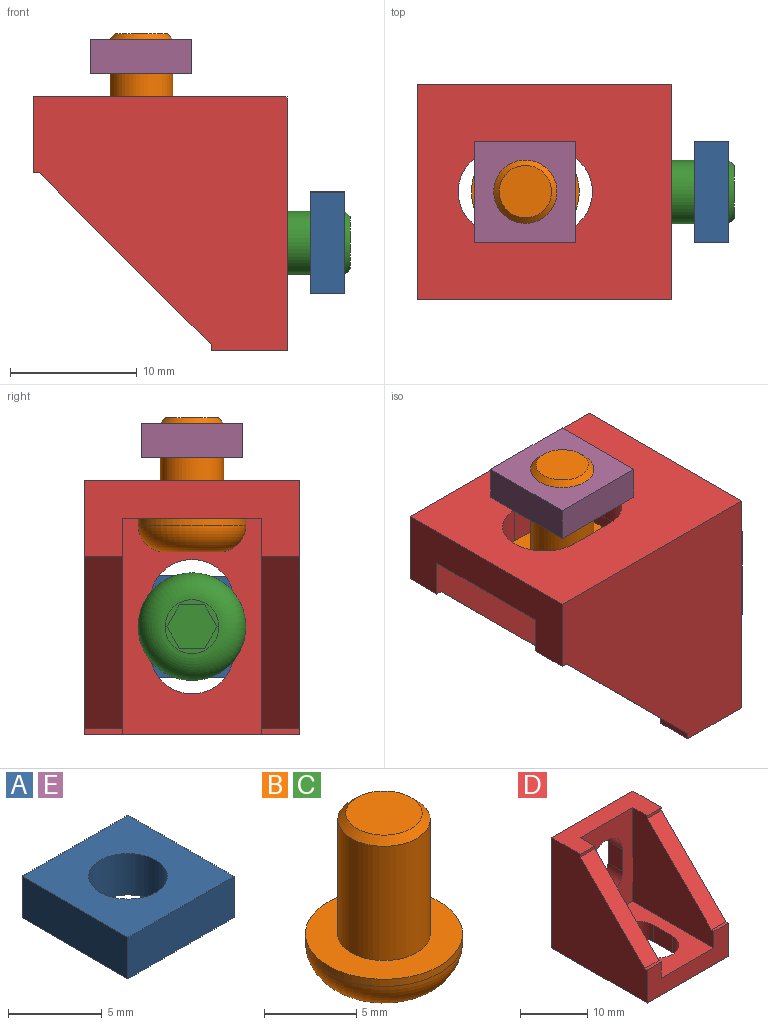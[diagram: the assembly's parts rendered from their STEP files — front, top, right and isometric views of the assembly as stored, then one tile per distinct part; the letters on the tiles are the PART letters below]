
ASSEMBLY  parts=5 mates=10
PART A: 7 faces, bbox 8x8x2.7 mm
  f0: plane 8x2.7mm, normal (0,-1,0), area 21.6mm2, adj f1,f4,f5,f6
  f1: plane 8x2.7mm, normal (1,0,0), area 21.6mm2, adj f0,f2,f5,f6
  f2: plane 8x2.7mm, normal (0,1,0), area 21.6mm2, adj f1,f4,f5,f6
  f3: cylinder r=2.1mm len=4.2mm, axis (0,0,-1), area 35.6mm2, adj f5,f6
  f4: plane 8x2.7mm, normal (-1,0,0), area 21.6mm2, adj f0,f2,f5,f6
  f5: plane 8x8mm, normal (0,0,1), area 50.1mm2, adj f0,f1,f2,f3,f4
  f6: plane 8x8mm, normal (0,0,-1), area 50.1mm2, adj f0,f1,f2,f3,f4
PART B: 14 faces, bbox 9.2x9.2x10.6 mm
  f0: plane 4.25x4.25mm, normal (0,0,-1), area 3.9mm2, adj f3,f4,f5,f6,f7,f8,f9
  f1: cylinder r=4.25mm len=8.5mm, axis (0,0,1), area 12.7mm2, adj f2,f3
  f2: plane 8.5x8.5mm, normal (0,0,1), area 37.1mm2, adj f1,f11
  f3: torus R=2.12mm, axis (0,0,-1), area 72.9mm2, adj f0,f1
  f4: plane 2.5x1.99mm, normal (-1,0,0), area 5mm2, adj f0,f5,f9,f10
  f5: plane 2.5x1.72mm, normal (-0.5,-0.87,0), area 5mm2, adj f0,f4,f6,f10
  f6: plane 2.5x1.72mm, normal (0.5,-0.87,0), area 5mm2, adj f0,f5,f7,f10
  f7: plane 2.5x1.99mm, normal (1,0,0), area 5mm2, adj f0,f6,f8,f10
  f8: plane 2.5x1.72mm, normal (0.5,0.87,0), area 5mm2, adj f0,f7,f9,f10
  f9: plane 2.5x1.72mm, normal (-0.5,0.87,0), area 5mm2, adj f0,f4,f8,f10
  f10: plane 3.97x3.44mm, normal (0,0,-1), area 10.2mm2, adj f4,f5,f6,f7,f8,f9
  f11: cylinder r=2.5mm len=7.57mm, axis (0,0,-1), area 118.9mm2, adj f2,f13
  f12: plane 4.13x4.13mm, normal (0,0,1), area 13.4mm2, adj f13
  f13: cone r=2.07mm half-angle=45deg, axis (0,0,-1), area 8.8mm2, adj f11,f12
PART C: same geometry as B
PART D: 24 faces, bbox 17x20x20 mm
  f0: plane 17x6mm, normal (0,0,1), area 69mm2, adj f3,f4,f5,f7,f8,f9,f12,f15
  f1: plane 17x11mm, normal (0,0,1), area 126.4mm2, adj f2,f7,f8,f9,f16,f17,f18,f19
  f2: plane 17x6mm, normal (0,-1,0), area 69mm2, adj f1,f3,f5,f6,f8,f9,f10,f14
  f3: plane 20x20mm, normal (1,0,0), area 295.1mm2, adj f0,f2,f4,f6,f13,f14,f15
  f4: plane 20x17mm, normal (0,1,0), area 279.4mm2, adj f0,f3,f5,f6,f20,f21,f22,f23
  f5: plane 20x20mm, normal (-1,0,0), area 295.1mm2, adj f0,f2,f4,f6,f10,f11,f12
  f6: plane 20x17mm, normal (0,0,-1), area 279.4mm2, adj f2,f3,f4,f5,f16,f17,f18,f19
  f7: plane 17x11mm, normal (0,-1,0), area 126.4mm2, adj f0,f1,f8,f9,f20,f21,f22,f23
  f8: plane 17x17mm, normal (-1,0,0), area 184.1mm2, adj f0,f1,f2,f7,f13,f14,f15
  f9: plane 17x17mm, normal (1,0,0), area 184.1mm2, adj f0,f1,f2,f7,f10,f11,f12
  f10: plane 3x0.5mm, normal (0,0,1), area 1.5mm2, adj f2,f5,f9,f11
  f11: plane 13.5x13.5mm, normal (0,-0.71,0.71), area 57.3mm2, adj f5,f9,f10,f12
  f12: plane 3x0.5mm, normal (0,-1,0), area 1.5mm2, adj f0,f5,f9,f11
  f13: plane 13.5x13.5mm, normal (0,-0.71,0.71), area 57.3mm2, adj f3,f8,f14,f15
  f14: plane 3x0.5mm, normal (0,0,1), area 1.5mm2, adj f2,f3,f8,f13
  f15: plane 3x0.5mm, normal (0,-1,0), area 1.5mm2, adj f0,f3,f8,f13
  f16: cylinder r=3.3mm len=6.6mm, axis (0,0,1), area 31.1mm2, adj f1,f6,f17,f19
  f17: plane 4x3mm, normal (1,0,0), area 12mm2, adj f1,f6,f16,f18
  f18: cylinder r=3.3mm len=6.6mm, axis (0,0,1), area 31.1mm2, adj f1,f6,f17,f19
  f19: plane 4x3mm, normal (-1,0,0), area 12mm2, adj f1,f6,f16,f18
  f20: cylinder r=3.3mm len=6.6mm, axis (0,-1,0), area 31.1mm2, adj f4,f7,f21,f23
  f21: plane 4x3mm, normal (-1,0,0), area 12mm2, adj f4,f7,f20,f22
  f22: cylinder r=3.3mm len=6.6mm, axis (0,-1,0), area 31.1mm2, adj f4,f7,f21,f23
  f23: plane 4x3mm, normal (1,0,0), area 12mm2, adj f4,f7,f20,f22
PART E: same geometry as A
PLACE A rot(axis=(0,1,0),90deg) t=(-41.83,0,-9.58)mm
PLACE B t=(-75.2,-20,-1.08)mm
PLACE C rot(axis=(0,1,0),90deg) t=(-46.7,-20,10.42)mm
PLACE D rot(axis=(0.71,0.71,0),180deg) t=(-53.7,-20,1.92)mm
PLACE E t=(-55.2,0,3.78)mm
MATE planar C.f1 <-> D.f7  axis (1,0,0) through (-46.7,-20,-9.58)mm
MATE cylindrical C.f1 <-> D.f7  axis (-1,0,0) through (-46.7,-20,-9.58)mm
MATE planar E.f5 <-> B.f1  axis (0,0,1) through (-55.2,-16,6.48)mm
MATE cylindrical B.f1 <-> E.f3  axis (0,0,-1) through (-55.2,-20,6.48)mm
MATE planar A.f3 <-> C.f1  axis (1,0,0) through (-39.13,-20,-9.58)mm
MATE cylindrical D.f1 <-> B.f1  axis (0,0,-1) through (-55.2,-20,-1.08)mm
MATE cylindrical C.f1 <-> A.f3  axis (-1,0,0) through (-39.13,-20,-9.58)mm
MATE parallel E.f1 <-> D.f4  axis (1,0,0) through (-51.2,-20,5.13)mm
MATE parallel A.f4 <-> D.f6  axis (0,0,1) through (-40.48,-20,-5.58)mm
MATE planar B.f1 <-> D.f1  axis (0,0,1) through (-55.2,-20,-1.08)mm
